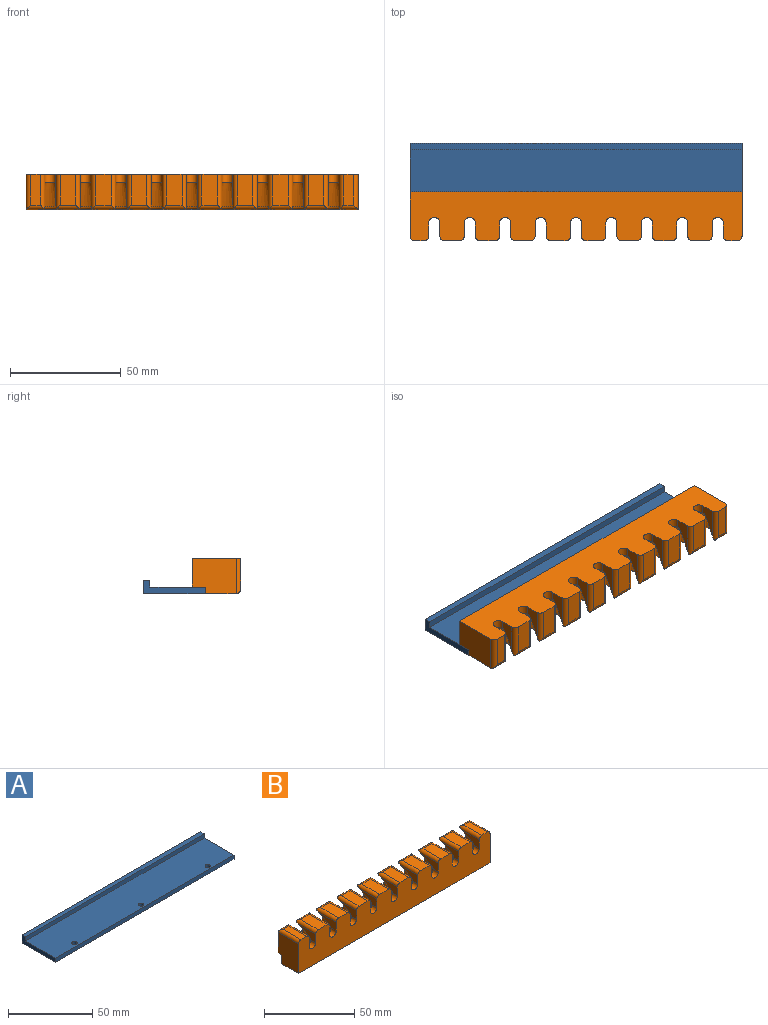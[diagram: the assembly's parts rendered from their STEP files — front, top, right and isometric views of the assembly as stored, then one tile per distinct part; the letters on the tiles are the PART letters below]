
ASSEMBLY  parts=2 mates=1
PART A: 11 faces, bbox 150x28x6 mm
  f0: plane 28x6mm, normal (1,0,0), area 93mm2, adj f1,f5,f7,f8,f9,f10
  f1: plane 150x6mm, normal (0,1,0), area 900mm2, adj f0,f2,f8,f10
  f2: plane 28x6mm, normal (-1,0,0), area 93mm2, adj f1,f5,f7,f8,f9,f10
  f3: cylinder r=1.6mm len=3.2mm, axis (0,0,-1), area 30.2mm2, adj f7,f8
  f4: cylinder r=1.6mm len=3.2mm, axis (0,0,-1), area 30.2mm2, adj f7,f8
  f5: plane 150x3mm, normal (0,-1,0), area 450mm2, adj f0,f2,f7,f8
  f6: cylinder r=1.6mm len=3.2mm, axis (0,0,-1), area 30.2mm2, adj f7,f8
  f7: plane 150x25mm, normal (0,0,1), area 3725.9mm2, adj f0,f2,f3,f4,f5,f6,f9
  f8: plane 150x28mm, normal (0,0,-1), area 4175.9mm2, adj f0,f1,f2,f3,f4,f5,f6
  f9: plane 150x3mm, normal (0,-1,0), area 450mm2, adj f0,f2,f7,f10
  f10: plane 150x3mm, normal (0,0,1), area 450mm2, adj f0,f1,f2,f9
PART B: 115 faces, bbox 150.2x16x24.3 mm
  f0: plane 8.5x4.25mm, normal (0,1,0), area 13.8mm2, adj f68,f103,f108
  f1: plane 8.5x4.25mm, normal (0,1,0), area 13.8mm2, adj f68,f100,f103
  f2: plane 8.5x4.25mm, normal (0,1,0), area 13.8mm2, adj f68,f97,f100
  f3: plane 8.5x4.25mm, normal (0,1,0), area 13.8mm2, adj f68,f93,f97
  f4: plane 8.5x4.25mm, normal (0,1,0), area 13.8mm2, adj f68,f89,f93
  f5: plane 8.5x4.25mm, normal (0,1,0), area 13.8mm2, adj f68,f85,f89
  f6: plane 8.5x4.25mm, normal (0,1,0), area 13.8mm2, adj f68,f81,f85
  f7: plane 8.5x4.25mm, normal (0,1,0), area 13.8mm2, adj f68,f77,f81
  f8: plane 14x7.25mm, normal (0,1,0), area 46.2mm2, adj f50,f68,f73,f77
  f9: plane 3.03x2.25mm, normal (0,1,0), area 3mm2, adj f76,f77,f81
  f10: plane 3.03x2.25mm, normal (0,1,0), area 3mm2, adj f80,f81,f85
  f11: plane 3.03x2.25mm, normal (0,1,0), area 3mm2, adj f84,f85,f89
  f12: plane 3.03x2.25mm, normal (0,1,0), area 3mm2, adj f88,f89,f93
  f13: plane 3.03x2.25mm, normal (0,1,0), area 3mm2, adj f92,f93,f97
  f14: plane 3.03x2.25mm, normal (0,1,0), area 3mm2, adj f96,f97,f100
  f15: plane 3.03x2.25mm, normal (0,1,0), area 3mm2, adj f99,f100,f103
  f16: plane 3.03x2.25mm, normal (0,1,0), area 3mm2, adj f103,f107,f108
  f17: plane 14x7.25mm, normal (0,1,0), area 46.2mm2, adj f49,f68,f104,f108
  f18: cylinder r=2.5mm len=5mm, axis (0,1,0), area 30.9mm2, adj f19,f20,f51,f67
  f19: plane 13.59x6mm, normal (1,0,0), area 46.6mm2, adj f18,f51,f67,f106
  f20: plane 13.59x6mm, normal (-1,0,0), area 46.6mm2, adj f18,f51,f67,f105
  f21: cylinder r=2.5mm len=5mm, axis (0,1,0), area 30.9mm2, adj f22,f23,f51,f66
  f22: plane 13.59x6mm, normal (1,0,0), area 46.6mm2, adj f21,f51,f66,f98
  f23: plane 13.59x6mm, normal (-1,0,0), area 46.6mm2, adj f21,f51,f66,f102
  f24: cylinder r=2.5mm len=5mm, axis (0,1,0), area 30.9mm2, adj f25,f26,f51,f65
  f25: plane 13.59x6mm, normal (1,0,0), area 46.6mm2, adj f24,f51,f65,f95
  f26: plane 13.59x6mm, normal (-1,0,0), area 46.6mm2, adj f24,f51,f65,f94
  f27: cylinder r=2.5mm len=5mm, axis (0,1,0), area 30.9mm2, adj f28,f29,f51,f64
  f28: plane 13.59x6mm, normal (1,0,0), area 46.6mm2, adj f27,f51,f64,f91
  f29: plane 13.59x6mm, normal (-1,0,0), area 46.6mm2, adj f27,f51,f64,f90
  f30: plane 13.59x6mm, normal (1,0,0), area 46.6mm2, adj f51,f54,f63,f87
  f31: plane 13.59x6mm, normal (-1,0,0), area 46.6mm2, adj f51,f54,f63,f86
  f32: plane 13.59x6mm, normal (1,0,0), area 46.6mm2, adj f51,f55,f62,f83
  f33: plane 13.59x6mm, normal (-1,0,0), area 46.6mm2, adj f51,f55,f62,f82
  f34: plane 13.59x6mm, normal (1,0,0), area 46.6mm2, adj f51,f56,f61,f79
  f35: plane 13.59x6mm, normal (-1,0,0), area 46.6mm2, adj f51,f56,f61,f78
  f36: plane 13.59x6mm, normal (1,0,0), area 46.6mm2, adj f51,f57,f60,f75
  f37: plane 13.59x6mm, normal (-1,0,0), area 46.6mm2, adj f51,f57,f60,f74
  f38: plane 13.59x6mm, normal (1,0,0), area 46.6mm2, adj f51,f58,f59,f72
  f39: plane 13.59x6mm, normal (-1,0,0), area 46.6mm2, adj f51,f58,f59,f71
  f40: plane 14x4.5mm, normal (0,0,1), area 63mm2, adj f51,f70,f72,f73
  f41: plane 14x7mm, normal (0,0,1), area 98mm2, adj f51,f71,f75,f76
  f42: plane 14x7mm, normal (0,0,1), area 98mm2, adj f51,f74,f79,f80
  f43: plane 14x7mm, normal (0,0,1), area 98mm2, adj f51,f78,f83,f84
  f44: plane 14x7mm, normal (0,0,1), area 98mm2, adj f51,f82,f87,f88
  f45: plane 14x7mm, normal (0,0,1), area 98mm2, adj f51,f86,f91,f92
  f46: plane 14x7mm, normal (0,0,1), area 98mm2, adj f51,f90,f95,f96
  f47: plane 14x7mm, normal (0,0,1), area 98mm2, adj f51,f94,f98,f99
  f48: plane 14x7mm, normal (0,0,1), area 98mm2, adj f51,f102,f106,f107
  f49: plane 20x16mm, normal (1,0,0), area 302mm2, adj f17,f51,f53,f68,f69,f101
  f50: plane 20x16mm, normal (-1,0,0), area 302mm2, adj f8,f51,f53,f68,f69,f70
  f51: plane 150x22mm, normal (0,-1,0), area 2834.5mm2, adj f18,f19,f20,f21,f22,f23,f24,f25
  f52: plane 14x4.5mm, normal (0,0,1), area 63mm2, adj f51,f101,f104,f105
  f53: plane 150x13mm, normal (0,0,-1), area 1950mm2, adj f49,f50,f51,f69
  f54: cylinder r=2.5mm len=5mm, axis (0,1,0), area 30.9mm2, adj f30,f31,f51,f63
  f55: cylinder r=2.5mm len=5mm, axis (0,1,0), area 30.9mm2, adj f32,f33,f51,f62
  f56: cylinder r=2.5mm len=5mm, axis (0,1,0), area 30.9mm2, adj f34,f35,f51,f61
  f57: cylinder r=2.5mm len=5mm, axis (0,1,0), area 30.9mm2, adj f36,f37,f51,f60
  f58: cylinder r=2.5mm len=5mm, axis (0,1,0), area 30.9mm2, adj f38,f39,f51,f59
  f59: cone r=2.5mm half-angle=22.5deg, axis (0,1,0), area 285.9mm2, adj f38,f39,f58,f71,f72,f77
  f60: cone r=2.5mm half-angle=22.5deg, axis (0,1,0), area 285.9mm2, adj f36,f37,f57,f74,f75,f81
  f61: cone r=2.5mm half-angle=22.5deg, axis (0,1,0), area 285.9mm2, adj f34,f35,f56,f78,f79,f85
  f62: cone r=2.5mm half-angle=22.5deg, axis (0,1,0), area 285.9mm2, adj f32,f33,f55,f82,f83,f89
  f63: cone r=2.5mm half-angle=22.5deg, axis (0,1,0), area 285.9mm2, adj f30,f31,f54,f86,f87,f93
  f64: cone r=2.5mm half-angle=22.5deg, axis (0,1,0), area 285.9mm2, adj f27,f28,f29,f90,f91,f97
  f65: cone r=2.5mm half-angle=22.5deg, axis (0,1,0), area 285.9mm2, adj f24,f25,f26,f94,f95,f100
  f66: cone r=2.5mm half-angle=22.5deg, axis (0,1,0), area 285.9mm2, adj f21,f22,f23,f98,f102,f103
  f67: cone r=2.5mm half-angle=22.5deg, axis (0,1,0), area 285.9mm2, adj f18,f19,f20,f105,f106,f108
  f68: plane 150x3mm, normal (0,0,-1), area 443.6mm2, adj f0,f1,f2,f3,f4,f5,f6,f7
  f69: plane 150x6mm, normal (0,1,0), area 881.5mm2, adj f49,f50,f53,f68,f110,f112,f114
  f70: cylinder r=2mm len=16mm, axis (0,1,0), area 47.1mm2, adj f40,f50,f51,f73
  f71: cylinder r=2mm len=15.64mm, axis (0,1,0), area 46.5mm2, adj f39,f41,f51,f59,f76,f77
  f72: cylinder r=2mm len=15.64mm, axis (0,-1,0), area 46.5mm2, adj f38,f40,f51,f59,f73,f77
  f73: cylinder r=2mm len=8.14mm, axis (1,0,0), area 18.6mm2, adj f8,f40,f70,f72,f77
  f74: cylinder r=2mm len=15.64mm, axis (0,1,0), area 46.5mm2, adj f37,f42,f51,f60,f80,f81
  f75: cylinder r=2mm len=15.64mm, axis (0,-1,0), area 46.5mm2, adj f36,f41,f51,f60,f76,f81
  f76: cylinder r=2mm len=10.28mm, axis (1,0,0), area 24.7mm2, adj f9,f41,f71,f75,f77,f81
  f77: torus R=8.84mm, axis (0,-1,0), area 88.2mm2, adj f7,f8,f9,f59,f68,f71,f72,f73
  f78: cylinder r=2mm len=15.64mm, axis (0,1,0), area 46.5mm2, adj f35,f43,f51,f61,f84,f85
  f79: cylinder r=2mm len=15.64mm, axis (0,-1,0), area 46.5mm2, adj f34,f42,f51,f61,f80,f85
  f80: cylinder r=2mm len=10.28mm, axis (1,0,0), area 24.7mm2, adj f10,f42,f74,f79,f81,f85
  f81: torus R=8.84mm, axis (0,-1,0), area 83.9mm2, adj f6,f7,f9,f10,f60,f68,f74,f75
  f82: cylinder r=2mm len=15.64mm, axis (0,1,0), area 46.5mm2, adj f33,f44,f51,f62,f88,f89
  f83: cylinder r=2mm len=15.64mm, axis (0,-1,0), area 46.5mm2, adj f32,f43,f51,f62,f84,f89
  f84: cylinder r=2mm len=10.28mm, axis (1,0,0), area 24.7mm2, adj f11,f43,f78,f83,f85,f89
  f85: torus R=8.84mm, axis (0,-1,0), area 83.9mm2, adj f5,f6,f10,f11,f61,f68,f78,f79
  f86: cylinder r=2mm len=15.64mm, axis (0,1,0), area 46.5mm2, adj f31,f45,f51,f63,f92,f93
  f87: cylinder r=2mm len=15.64mm, axis (0,-1,0), area 46.5mm2, adj f30,f44,f51,f63,f88,f93
  f88: cylinder r=2mm len=10.28mm, axis (1,0,0), area 24.7mm2, adj f12,f44,f82,f87,f89,f93
  f89: torus R=8.84mm, axis (0,-1,0), area 83.9mm2, adj f4,f5,f11,f12,f62,f68,f82,f83
  f90: cylinder r=2mm len=15.64mm, axis (0,1,0), area 46.5mm2, adj f29,f46,f51,f64,f96,f97
  f91: cylinder r=2mm len=15.64mm, axis (0,-1,0), area 46.5mm2, adj f28,f45,f51,f64,f92,f97
  f92: cylinder r=2mm len=10.28mm, axis (1,0,0), area 24.7mm2, adj f13,f45,f86,f91,f93,f97
  f93: torus R=8.84mm, axis (0,-1,0), area 83.9mm2, adj f3,f4,f12,f13,f63,f68,f86,f87
  f94: cylinder r=2mm len=15.64mm, axis (0,1,0), area 46.5mm2, adj f26,f47,f51,f65,f99,f100
  f95: cylinder r=2mm len=15.64mm, axis (0,-1,0), area 46.5mm2, adj f25,f46,f51,f65,f96,f100
  f96: cylinder r=2mm len=10.28mm, axis (1,0,0), area 24.7mm2, adj f14,f46,f90,f95,f97,f100
  f97: torus R=8.84mm, axis (0,-1,0), area 83.9mm2, adj f2,f3,f13,f14,f64,f68,f90,f91
  f98: cylinder r=2mm len=15.64mm, axis (0,-1,0), area 46.5mm2, adj f22,f47,f51,f66,f99,f103
  f99: cylinder r=2mm len=10.28mm, axis (1,0,0), area 24.7mm2, adj f15,f47,f94,f98,f100,f103
  f100: torus R=8.84mm, axis (0,-1,0), area 83.9mm2, adj f1,f2,f14,f15,f65,f68,f94,f95
  f101: cylinder r=2mm len=16mm, axis (0,-1,0), area 47.1mm2, adj f49,f51,f52,f104
  f102: cylinder r=2mm len=15.64mm, axis (0,1,0), area 46.5mm2, adj f23,f48,f51,f66,f103,f107
  f103: torus R=8.84mm, axis (0,-1,0), area 83.9mm2, adj f0,f1,f15,f16,f66,f68,f98,f99
  f104: cylinder r=2mm len=8.14mm, axis (1,0,0), area 18.6mm2, adj f17,f52,f101,f105,f108
  f105: cylinder r=2mm len=15.64mm, axis (0,1,0), area 46.5mm2, adj f20,f51,f52,f67,f104,f108
  f106: cylinder r=2mm len=15.64mm, axis (0,-1,0), area 46.5mm2, adj f19,f48,f51,f67,f107,f108
  f107: cylinder r=2mm len=10.28mm, axis (1,0,0), area 24.7mm2, adj f16,f48,f102,f103,f106,f108
  f108: torus R=8.84mm, axis (0,-1,0), area 88.2mm2, adj f0,f16,f17,f67,f68,f103,f104,f105
  f109: cone r=0mm half-angle=59deg, axis (0,1,0), area 7.2mm2, adj f110
  f110: cylinder r=1.4mm len=10mm, axis (0,1,0), area 88mm2, adj f69,f109
  f111: cone r=0mm half-angle=59deg, axis (0,1,0), area 7.2mm2, adj f112
  f112: cylinder r=1.4mm len=10mm, axis (0,1,0), area 88mm2, adj f69,f111
  f113: cone r=0mm half-angle=59deg, axis (0,1,0), area 7.2mm2, adj f114
  f114: cylinder r=1.4mm len=10mm, axis (0,1,0), area 88mm2, adj f69,f113
PLACE A t=(1.74,16.93,-51.29)mm
PLACE B rot(axis=(0,-0.71,0.71),180deg) t=(1.74,8.93,-43.29)mm
MATE fastened B.f112 <-> A.f4  axis (0,0,-1) through (1.74,5.93,-48.29)mm
